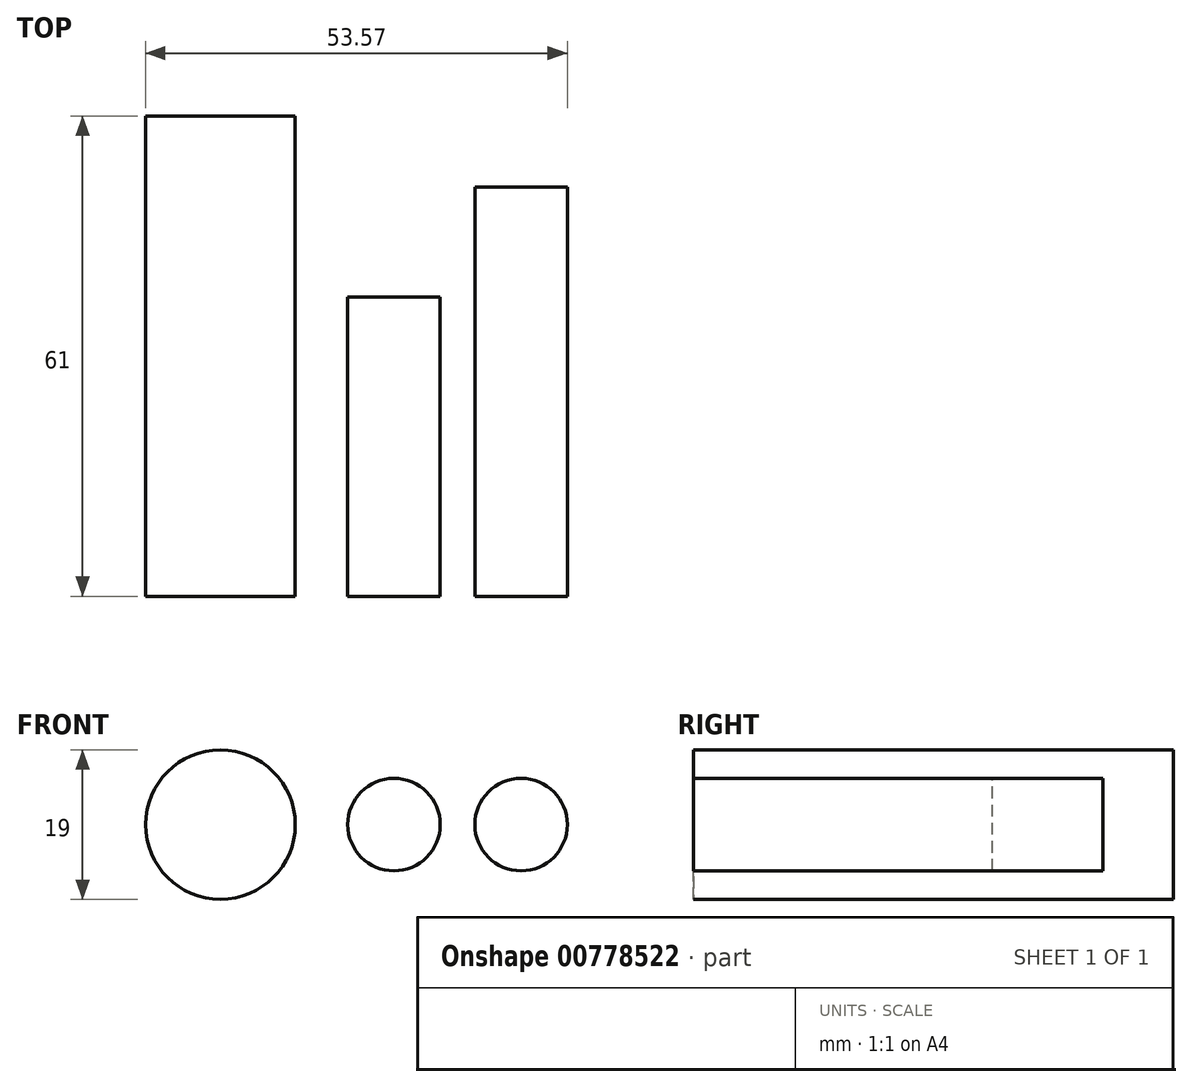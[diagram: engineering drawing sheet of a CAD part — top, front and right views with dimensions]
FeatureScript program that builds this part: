
annotation { "Feature Type Name" : "Feature", "Feature Type Description" : "" }
export const myFeature = defineFeature(function(context is Context, id is Id, definition is map)
    precondition{}
    {
        {
            var Q0;
            Q0=qCreatedBy(makeId("Front.planeOp"),FACE);
            var sketch = newSketch(context, id + "F0", { "sketchPlane" : qUnion([Q0])});
            skCircle(sketch, "E0", {"center": v(-118.45, 0) * mm, "radius": 9.5 * mm});
            skCircle(sketch, "E1", {"center": v(-96.4, 0) * mm, "radius": 5.88 * mm});
            skCircle(sketch, "E2", {"center": v(-80.26, 0) * mm, "radius": 5.88 * mm});
            skSolve(sketch);
        }
        {
            var Q0;
            Q0=makeQuery(id+"F0.imprint","IMPRINT",FACE,{"disambiguationData":[TD([[makeQuery(id+"F0.imprint","IMPRINT",EDGE,{"derivedFrom":sQuery(id+"F0.wireOp",EDGE,"E0")}),1.0]])]});
            extrude(context, id + "F1", {"entities" : qUnion([Q0]), "oppositeDirection" : true, "depth" : 61 * mm, "offsetDistance" : 25 * mm});
        }
        {
            var Q0;
            Q0=makeQuery(id+"F0.imprint","IMPRINT",FACE,{"disambiguationData":[TD([[makeQuery(id+"F0.imprint","IMPRINT",EDGE,{"derivedFrom":sQuery(id+"F0.wireOp",EDGE,"E1")}),1.0]])]});
            extrude(context, id + "F2", {"entities" : qUnion([Q0]), "oppositeDirection" : true, "depth" : 38 * mm, "offsetDistance" : 25 * mm});
        }
        {
            var Q0;
            Q0=makeQuery(id+"F0.imprint","IMPRINT",FACE,{"disambiguationData":[TD([[makeQuery(id+"F0.imprint","IMPRINT",EDGE,{"derivedFrom":sQuery(id+"F0.wireOp",EDGE,"E2")}),1.0]])]});
            extrude(context, id + "F3", {"entities" : qUnion([Q0]), "oppositeDirection" : true, "depth" : 52 * mm, "offsetDistance" : 25 * mm});
        }
    });
